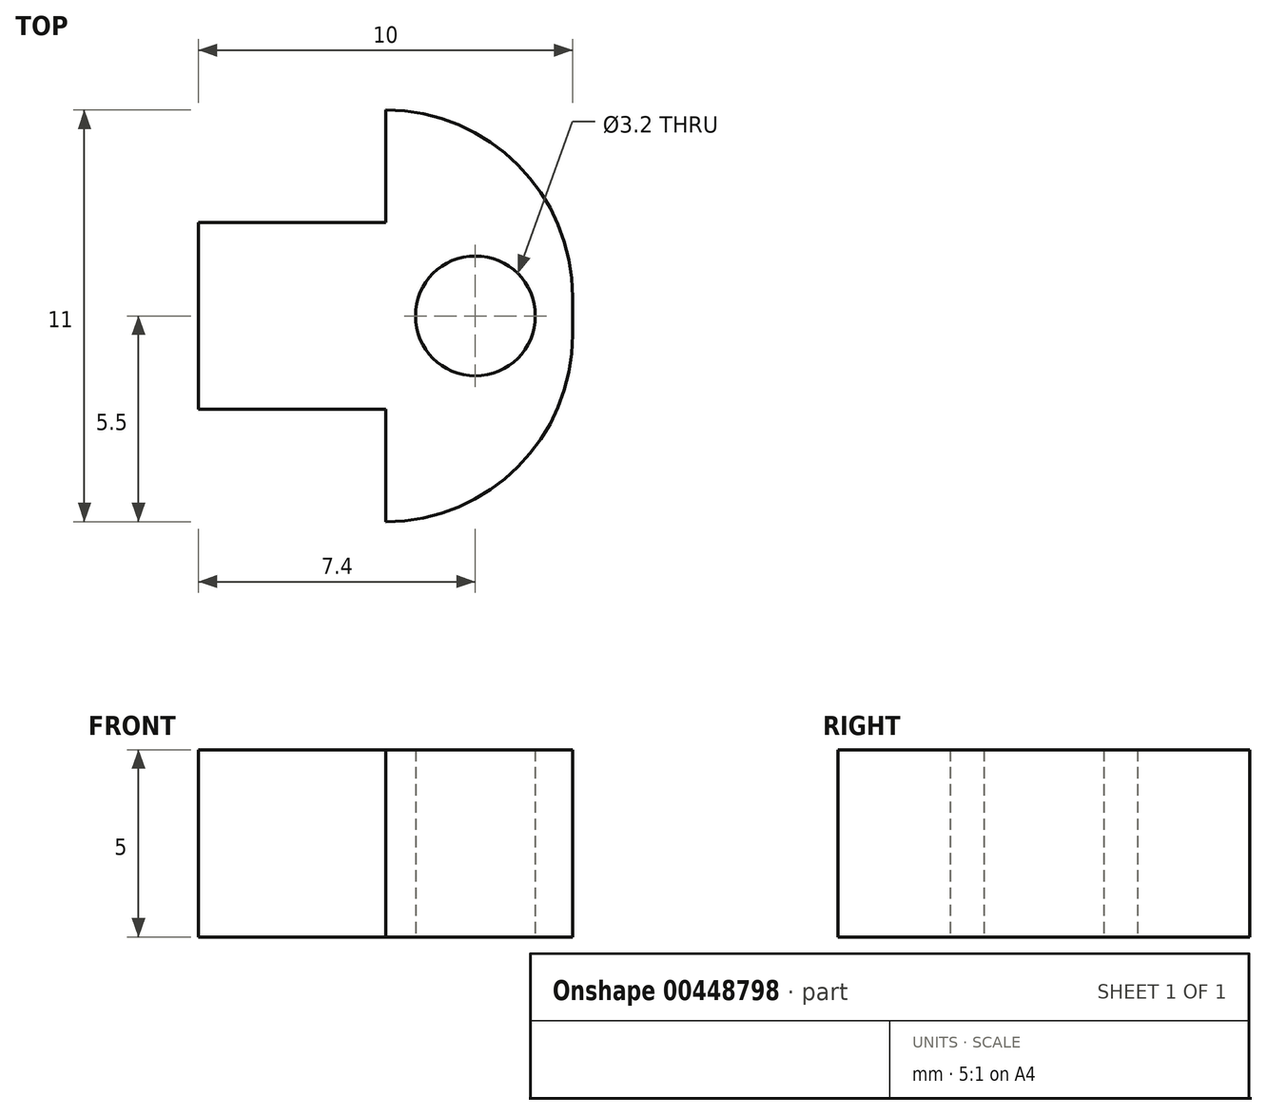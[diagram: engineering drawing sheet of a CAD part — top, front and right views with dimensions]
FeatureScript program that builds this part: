
annotation { "Feature Type Name" : "Feature", "Feature Type Description" : "" }
export const myFeature = defineFeature(function(context is Context, id is Id, definition is map)
    precondition{}
    {
        {
            var Q0;
            Q0=qCreatedBy(makeId("Top.planeOp"),FACE);
            var sketch = newSketch(context, id + "F0", { "sketchPlane" : qUnion([Q0])});
            skLineSegment(sketch, "E0.bottom", {"start": v(0, 0) * mm, "end": v(5, 0) * mm});
            skLineSegment(sketch, "E0.top", {"start": v(0, 5) * mm, "end": v(5, 5) * mm});
            skLineSegment(sketch, "E0.left", {"start": v(0, 0) * mm, "end": v(0, 5) * mm});
            skLineSegment(sketch, "E0.right", {"start": v(10, 2) * mm, "end": v(10, 3) * mm});
            skLineSegment(sketch, "E1", {"start": v(5, 5) * mm, "end": v(5, 0) * mm, "construction": true});
            skCircle(sketch, "E2", {"center": v(7.4, 2.5) * mm, "radius": 1.6 * mm});
            skPoint(sketch, "E2.centerSnap0", {"position": v(5, 2.5) * mm});
            skLineSegment(sketch, "E3", {"start": v(5, 5) * mm, "end": v(5, 8) * mm});
            skLineSegment(sketch, "E4", {"start": v(5, 8) * mm, "end": v(5, 8) * mm});
            skLineSegment(sketch, "E5", {"start": v(5, 0) * mm, "end": v(5, -3) * mm});
            skLineSegment(sketch, "E6", {"start": v(5, -3) * mm, "end": v(5, -3) * mm});
            skPoint(sketch, "E7.visualSharp", {"position": v(10, -3) * mm});
            skArc(sketch, "E7.filletArc", {"start": v(5, -3) * mm, "mid": v(8.54, -1.54) * mm, "end": v(10, 2) * mm});
            skPoint(sketch, "E8.visualSharp", {"position": v(10, 8) * mm});
            skArc(sketch, "E8.filletArc", {"start": v(10, 3) * mm, "mid": v(8.54, 6.54) * mm, "end": v(5, 8) * mm});
            skSolve(sketch);
        }
        {
            var Q0;
            Q0=makeQuery(id+"F0.imprint","IMPRINT",FACE,{"disambiguationData":[TD([[makeQuery(id+"F0.imprint","IMPRINT",EDGE,{"derivedFrom":sQuery(id+"F0.wireOp",EDGE,"E0.bottom")}),1.0]])]});
            extrude(context, id + "F1", {"entities" : qUnion([Q0]), "depth" : 5 * mm});
        }
    });
